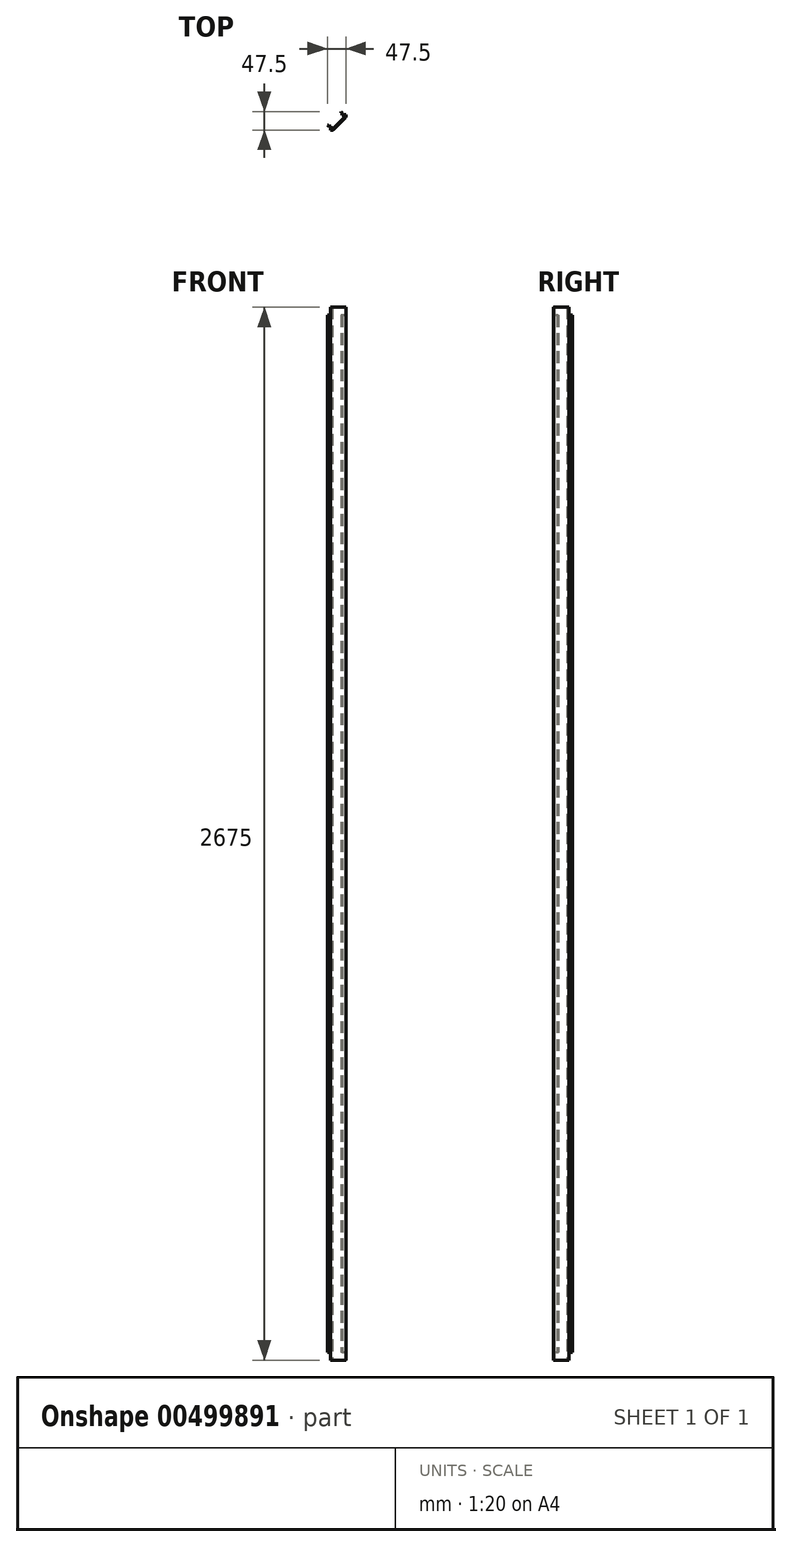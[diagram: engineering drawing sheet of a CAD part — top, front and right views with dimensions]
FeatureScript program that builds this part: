
annotation { "Feature Type Name" : "Feature", "Feature Type Description" : "" }
export const myFeature = defineFeature(function(context is Context, id is Id, definition is map)
    precondition{}
    {
        {
            var Q0;
            Q0=qCreatedBy(makeId("Top.planeOp"),FACE);
            var sketch = newSketch(context, id + "F0", { "sketchPlane" : qUnion([Q0])});
            skLineSegment(sketch, "E0", {"start": v(-68.1, 0) * mm, "end": v(72.16, 0) * mm, "construction": true});
            skLineSegment(sketch, "E1", {"start": v(0, 70.28) * mm, "end": v(0, -61.88) * mm, "construction": true});
            skLineSegment(sketch, "E2.bottom", {"start": v(-19.75, 19.75) * mm, "end": v(19.75, 19.75) * mm, "construction": true});
            skLineSegment(sketch, "E2.top", {"start": v(-19.75, -19.75) * mm, "end": v(19.75, -19.75) * mm, "construction": true});
            skLineSegment(sketch, "E2.left", {"start": v(-19.75, 19.75) * mm, "end": v(-19.75, -19.75) * mm, "construction": true});
            skLineSegment(sketch, "E2.right", {"start": v(19.75, 19.75) * mm, "end": v(19.75, -19.75) * mm, "construction": true});
            skLineSegment(sketch, "E3", {"start": v(-19.75, -19.75) * mm, "end": v(-13.75, -19.75) * mm});
            skLineSegment(sketch, "E4", {"start": v(19.75, 19.75) * mm, "end": v(19.75, 13.75) * mm});
            skLineSegment(sketch, "E5", {"start": v(-13.75, -19.75) * mm, "end": v(19.75, 13.75) * mm});
            skLineSegment(sketch, "E6.0", {"start": v(-19.75, -17.75) * mm, "end": v(-14.58, -17.75) * mm});
            skLineSegment(sketch, "E6.1", {"start": v(-14.58, -17.75) * mm, "end": v(17.75, 14.58) * mm});
            skLineSegment(sketch, "E6.2", {"start": v(17.75, 19.75) * mm, "end": v(17.75, 14.58) * mm});
            skLineSegment(sketch, "E7", {"start": v(-19.75, -19.75) * mm, "end": v(-19.75, -17.75) * mm});
            skLineSegment(sketch, "E8", {"start": v(19.75, 19.75) * mm, "end": v(17.75, 19.75) * mm});
            skSolve(sketch);
        }
        {
            var Q0;
            Q0=qSketchRegion(id+"F0",true);
            extrude(context, id + "F1", {"entities" : qUnion([Q0]), "depth" : 20 * mm});
        }
        {
            var Q0;
            Q0=makeQuery(id+"F1.opExtrude","CAP_FACE",FACE,{"disambiguationData":[OSD([sQuery(id+"F0.wireOp",EDGE,"E3"),sQuery(id+"F0.wireOp",EDGE,"E4"),sQuery(id+"F0.wireOp",EDGE,"E5"),sQuery(id+"F0.wireOp",EDGE,"E6.0"),sQuery(id+"F0.wireOp",EDGE,"E6.1"),sQuery(id+"F0.wireOp",EDGE,"E6.2"),sQuery(id+"F0.wireOp",EDGE,"E7"),sQuery(id+"F0.wireOp",EDGE,"E8")])],"isStart":false});
            var sketch = newSketch(context, id + "F2", { "sketchPlane" : qUnion([Q0])});
            skLineSegment(sketch, "E9.1", {"start": v(-13.75, -19.75) * mm, "end": v(19.75, 13.75) * mm});
            skLineSegment(sketch, "E9.2", {"start": v(19.75, 19.75) * mm, "end": v(19.75, 13.75) * mm});
            skLineSegment(sketch, "E10", {"start": v(19.75, 19.75) * mm, "end": v(11.25, 19.75) * mm});
            skLineSegment(sketch, "E11", {"start": v(17.75, 17.75) * mm, "end": v(17.75, 14.58) * mm});
            skLineSegment(sketch, "E12", {"start": v(17.75, 14.58) * mm, "end": v(14.34, 11.16) * mm});
            skLineSegment(sketch, "E13.left", {"start": v(11.25, 19.75) * mm, "end": v(11.25, 23.75) * mm});
            skLineSegment(sketch, "E14", {"start": v(11.25, 23.75) * mm, "end": v(7.25, 27.75) * mm});
            skLineSegment(sketch, "E15.trimOffspring", {"start": v(14.34, 11.16) * mm, "end": v(-11.16, -14.34) * mm});
            skLineSegment(sketch, "E16.0", {"start": v(9.25, 19.75) * mm, "end": v(9.25, 22.92) * mm});
            skLineSegment(sketch, "E17.0", {"start": v(9.25, 22.92) * mm, "end": v(7.25, 24.92) * mm});
            skLineSegment(sketch, "E18.trimOffspring", {"start": v(7.25, 24.92) * mm, "end": v(7.25, 27.75) * mm});
            skLineSegment(sketch, "E19", {"start": v(0, 0) * mm, "end": v(3, -3) * mm, "construction": true});
            skLineSegment(sketch, "E20.MirrorCS", {"start": v(-19.75, -9.25) * mm, "end": v(-22.92, -9.25) * mm});
            skLineSegment(sketch, "E21.MirrorCS", {"start": v(-19.75, -11.25) * mm, "end": v(-23.75, -11.25) * mm});
            skLineSegment(sketch, "E22.MirrorCS", {"start": v(-24.92, -7.25) * mm, "end": v(-27.75, -7.25) * mm});
            skLineSegment(sketch, "E23.MirrorCS", {"start": v(-19.75, -19.75) * mm, "end": v(-13.75, -19.75) * mm});
            skLineSegment(sketch, "E24.MirrorCS", {"start": v(-14.58, -17.75) * mm, "end": v(-11.16, -14.34) * mm});
            skLineSegment(sketch, "E25.MirrorCS", {"start": v(-23.75, -11.25) * mm, "end": v(-27.75, -7.25) * mm});
            skLineSegment(sketch, "E26.MirrorCS", {"start": v(-17.75, -17.75) * mm, "end": v(-14.58, -17.75) * mm});
            skLineSegment(sketch, "E27.MirrorCS", {"start": v(-22.92, -9.25) * mm, "end": v(-24.92, -7.25) * mm});
            skLineSegment(sketch, "E28.MirrorCS", {"start": v(-19.75, -19.75) * mm, "end": v(-19.75, -11.25) * mm});
            skLineSegment(sketch, "E29.trimOffspring", {"start": v(-11.16, -14.34) * mm, "end": v(-14.58, -17.75) * mm});
            skLineSegment(sketch, "E30", {"start": v(9.25, 19.75) * mm, "end": v(9.25, 17.75) * mm});
            skLineSegment(sketch, "E31", {"start": v(9.25, 17.75) * mm, "end": v(17.75, 17.75) * mm});
            skLineSegment(sketch, "E32", {"start": v(-19.75, -9.25) * mm, "end": v(-17.75, -9.25) * mm});
            skLineSegment(sketch, "E33", {"start": v(-17.75, -9.25) * mm, "end": v(-17.75, -17.75) * mm});
            skSolve(sketch);
        }
        {
            var Q0;
            Q0=qSketchRegion(id+"F2",true);
            extrude(context, id + "F3", {"entities" : qUnion([Q0]), "operationType" : NewBodyOperationType.ADD, "depth" : 2635 * mm});
        }
        {
            var Q0;
            Q0=makeQuery(id+"F3.opExtrude","CAP_FACE",FACE,{"disambiguationData":[OSD([sQuery(id+"F2.wireOp",EDGE,"E9.1"),sQuery(id+"F2.wireOp",EDGE,"E9.2"),sQuery(id+"F2.wireOp",EDGE,"E10"),sQuery(id+"F2.wireOp",EDGE,"E11"),sQuery(id+"F2.wireOp",EDGE,"E12"),sQuery(id+"F2.wireOp",EDGE,"E13.left"),sQuery(id+"F2.wireOp",EDGE,"E14"),sQuery(id+"F2.wireOp",EDGE,"E15.trimOffspring"),sQuery(id+"F2.wireOp",EDGE,"E16.0"),sQuery(id+"F2.wireOp",EDGE,"E17.0"),sQuery(id+"F2.wireOp",EDGE,"E18.trimOffspring"),sQuery(id+"F2.wireOp",EDGE,"E20.MirrorCS"),sQuery(id+"F2.wireOp",EDGE,"E21.MirrorCS"),sQuery(id+"F2.wireOp",EDGE,"E22.MirrorCS"),sQuery(id+"F2.wireOp",EDGE,"E23.MirrorCS"),sQuery(id+"F2.wireOp",EDGE,"E25.MirrorCS"),sQuery(id+"F2.wireOp",EDGE,"E26.MirrorCS"),sQuery(id+"F2.wireOp",EDGE,"E27.MirrorCS"),sQuery(id+"F2.wireOp",EDGE,"E28.MirrorCS"),sQuery(id+"F2.wireOp",EDGE,"E29.trimOffspring"),sQuery(id+"F2.wireOp",EDGE,"E30"),sQuery(id+"F2.wireOp",EDGE,"E31"),sQuery(id+"F2.wireOp",EDGE,"E32"),sQuery(id+"F2.wireOp",EDGE,"E33")])],"isStart":false});
            var sketch = newSketch(context, id + "F4", { "sketchPlane" : qUnion([Q0])});
            skLineSegment(sketch, "E34.0.0", {"start": v(19.75, 19.75) * mm, "end": v(19.75, 13.75) * mm});
            skLineSegment(sketch, "E34.0.1", {"start": v(19.75, 13.75) * mm, "end": v(-13.75, -19.75) * mm});
            skLineSegment(sketch, "E34.0.2", {"start": v(-13.75, -19.75) * mm, "end": v(-19.75, -19.75) * mm});
            skLineSegment(sketch, "E34.0.3", {"start": v(-19.75, -19.75) * mm, "end": v(-19.75, -17.75) * mm});
            skLineSegment(sketch, "E34.0.4", {"start": v(-19.75, -17.75) * mm, "end": v(-14.58, -17.75) * mm});
            skLineSegment(sketch, "E34.0.5", {"start": v(-14.58, -17.75) * mm, "end": v(17.75, 14.58) * mm});
            skLineSegment(sketch, "E34.0.6", {"start": v(17.75, 14.58) * mm, "end": v(17.75, 19.75) * mm});
            skLineSegment(sketch, "E34.0.7", {"start": v(17.75, 19.75) * mm, "end": v(19.75, 19.75) * mm});
            skSolve(sketch);
        }
        {
            var Q0;
            Q0=qSketchRegion(id+"F4",true);
            extrude(context, id + "F5", {"entities" : qUnion([Q0]), "operationType" : NewBodyOperationType.ADD, "depth" : 20 * mm});
        }
        {
            var Q0;
            Q0=makeQuery(id+"F5.boolean.opBoolean","MERGE",EDGE,{"derivedFrom":[makeQuery(id+"F3.boolean.opBoolean","MERGE",EDGE,{"derivedFrom":[makeQuery(id+"F1.opExtrude","SWEPT_EDGE",EDGE,{"disambiguationData":[OSD([sQuery(id+"F0.wireOp",EDGE,"E4"),sQuery(id+"F0.wireOp",EDGE,"E5")])]}),makeQuery(id+"F3.opExtrude","SWEPT_EDGE",EDGE,{"disambiguationData":[OSD([sQuery(id+"F2.wireOp",EDGE,"E9.1"),sQuery(id+"F2.wireOp",EDGE,"E9.2")])]})]}),makeQuery(id+"F5.opExtrude","SWEPT_EDGE",EDGE,{"disambiguationData":[OSD([sQuery(id+"F4.wireOp",EDGE,"E34.0.0"),sQuery(id+"F4.wireOp",EDGE,"E34.0.1")])]})]});
            var Q1;
            Q1=makeQuery(id+"F5.boolean.opBoolean","MERGE",EDGE,{"derivedFrom":[makeQuery(id+"F3.boolean.opBoolean","MERGE",EDGE,{"derivedFrom":[makeQuery(id+"F1.opExtrude","SWEPT_EDGE",EDGE,{"disambiguationData":[OSD([sQuery(id+"F0.wireOp",EDGE,"E3"),sQuery(id+"F0.wireOp",EDGE,"E5")])]}),makeQuery(id+"F3.opExtrude","SWEPT_EDGE",EDGE,{"disambiguationData":[OSD([sQuery(id+"F2.wireOp",EDGE,"E9.1"),sQuery(id+"F2.wireOp",EDGE,"E23.MirrorCS")])]})]}),makeQuery(id+"F5.opExtrude","SWEPT_EDGE",EDGE,{"disambiguationData":[OSD([sQuery(id+"F4.wireOp",EDGE,"E34.0.1"),sQuery(id+"F4.wireOp",EDGE,"E34.0.2")])]})]});
            fillet(context, id + "F6", {"entities" : qUnion([Q0, Q1]), "radius" : 5 * mm, "tangentPropagation" : true, "allowEdgeOverflow" : false});
        }
    });
